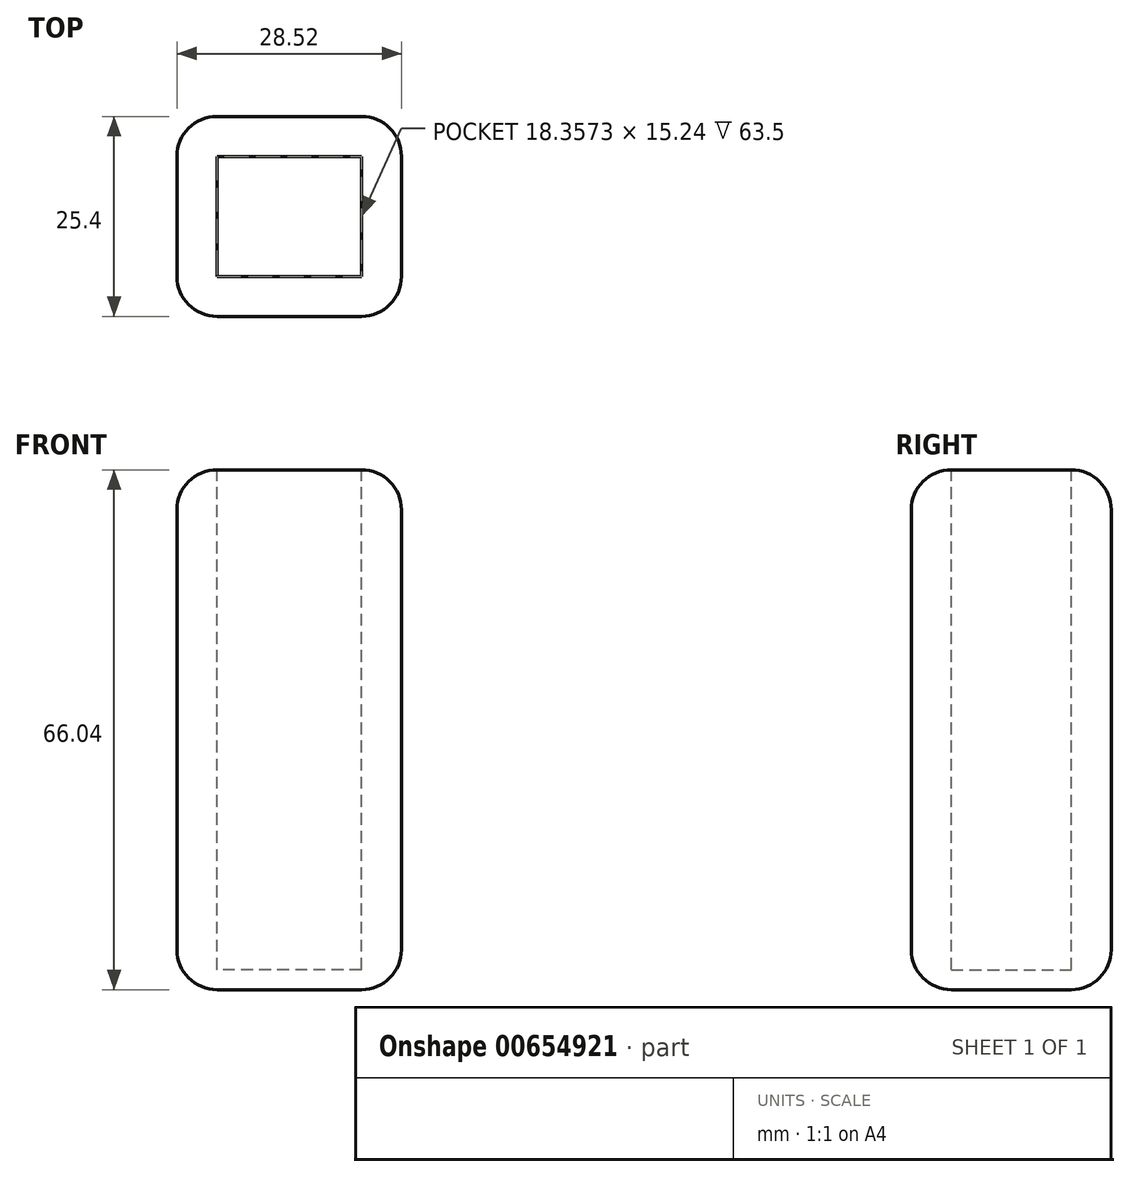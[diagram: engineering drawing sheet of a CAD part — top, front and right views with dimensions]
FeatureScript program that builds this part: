
annotation { "Feature Type Name" : "Feature", "Feature Type Description" : "" }
export const myFeature = defineFeature(function(context is Context, id is Id, definition is map)
    precondition{}
    {
        {
            var Q0;
            Q0=qCreatedBy(makeId("Front.planeOp"),FACE);
            var sketch = newSketch(context, id + "F0", { "sketchPlane" : qUnion([Q0])});
            skLineSegment(sketch, "E0", {"start": v(0, 0) * mm, "end": v(28.52, 0) * mm});
            skLineSegment(sketch, "E1", {"start": v(28.52, 0) * mm, "end": v(28.52, 66.04) * mm});
            skLineSegment(sketch, "E2", {"start": v(28.52, 66.04) * mm, "end": v(0, 66.04) * mm});
            skLineSegment(sketch, "E3", {"start": v(0, 66.04) * mm, "end": v(0, 0) * mm});
            skSolve(sketch);
        }
        {
            var Q0;
            Q0 = qSketchRegion(id + "F0", true);
            extrude(context, id + "F1", {"entities" : qUnion([Q0]), "depth" : 25.4 * mm, "offsetDistance" : 25.4 * mm});
        }
        {
            var Q0;
            Q0=makeQuery(id+"F1.opExtrude","CAP_FACE",FACE,{"disambiguationData":[OSD([sQuery(id+"F0.wireOp",EDGE,"E0"),sQuery(id+"F0.wireOp",EDGE,"E1"),sQuery(id+"F0.wireOp",EDGE,"E2"),sQuery(id+"F0.wireOp",EDGE,"E3")])],"isStart":false});
            var Q1;
            Q1=makeQuery(id+"F1.opExtrude","SWEPT_FACE",FACE,{"disambiguationData":[OSD([sQuery(id+"F0.wireOp",EDGE,"E1")])]});
            var Q2;
            Q2=makeQuery(id+"F1.opExtrude","SWEPT_FACE",FACE,{"disambiguationData":[OSD([sQuery(id+"F0.wireOp",EDGE,"E2")])]});
            var Q3;
            Q3=makeQuery(id+"F1.opExtrude","SWEPT_FACE",FACE,{"disambiguationData":[OSD([sQuery(id+"F0.wireOp",EDGE,"E0")])]});
            var Q4;
            Q4=makeQuery(id+"F1.opExtrude","CAP_EDGE",EDGE,{"disambiguationData":[OSD([sQuery(id+"F0.wireOp",EDGE,"E3")])],"isStart":true});
            fillet(context, id + "F2", {"entities" : qUnion([Q0, Q1, Q2, Q3, Q4]), "radius" : 5.08 * mm, "tangentPropagation" : true, "allowEdgeOverflow" : false});
        }
        {
            var Q0;
            Q0=makeQuery(id+"F1.opExtrude","SWEPT_FACE",FACE,{"disambiguationData":[OSD([sQuery(id+"F0.wireOp",EDGE,"E2")])]});
            extrude(context, id + "F3", {"entities" : qUnion([Q0]), "operationType" : NewBodyOperationType.REMOVE, "oppositeDirection" : true, "depth" : 63.5 * mm, "offsetDistance" : 25.4 * mm});
        }
    });
